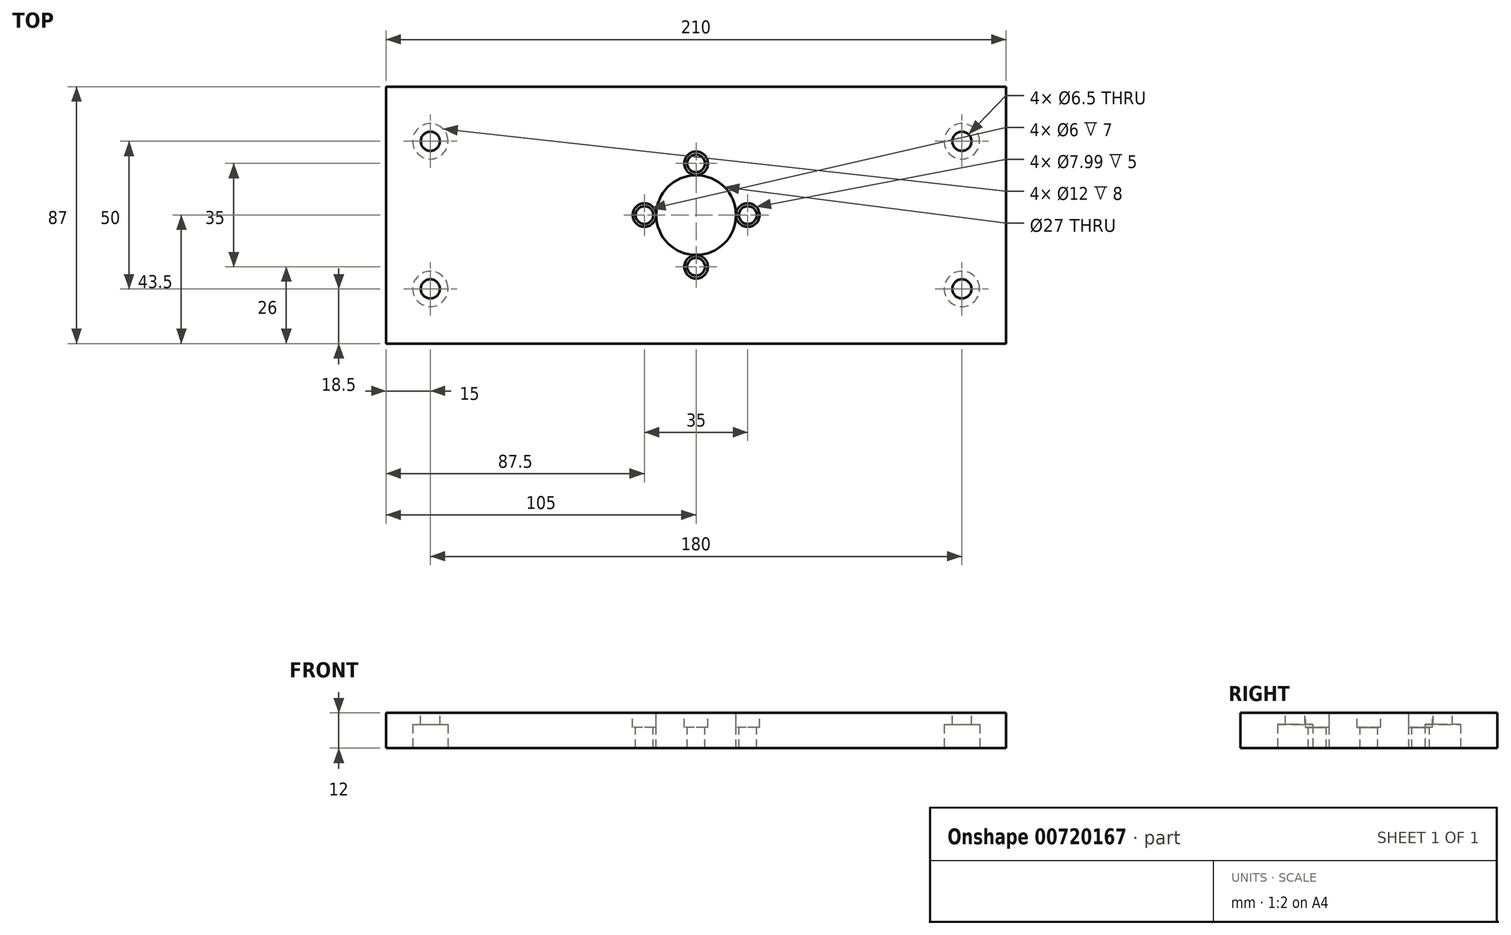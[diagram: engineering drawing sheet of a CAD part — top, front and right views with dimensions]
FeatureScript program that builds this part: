
annotation { "Feature Type Name" : "Feature", "Feature Type Description" : "" }
export const myFeature = defineFeature(function(context is Context, id is Id, definition is map)
    precondition{}
    {
        {
            var Q0;
            Q0=qCreatedBy(makeId("Top.planeOp"),FACE);
            var sketch = newSketch(context, id + "F0", { "sketchPlane" : qUnion([Q0])});
            skLineSegment(sketch, "E0.bottom", {"start": v(0, 0) * mm, "end": v(210, 0) * mm});
            skLineSegment(sketch, "E0.top", {"start": v(0, 87) * mm, "end": v(210, 87) * mm});
            skLineSegment(sketch, "E0.left", {"start": v(0, 0) * mm, "end": v(0, 87) * mm});
            skLineSegment(sketch, "E0.right", {"start": v(210, 0) * mm, "end": v(210, 87) * mm});
            skSolve(sketch);
        }
        {
            var Q0;
            Q0=makeQuery(id+"F0.imprint","IMPRINT",FACE,{"disambiguationData":[TD([[makeQuery(id+"F0.imprint","IMPRINT",EDGE,{"derivedFrom":sQuery(id+"F0.wireOp",EDGE,"E0.bottom")}),1.0]])]});
            extrude(context, id + "F1", {"entities" : qUnion([Q0]), "depth" : 12 * mm, "offsetDistance" : 25 * mm});
        }
        {
            var Q0;
            Q0=makeQuery(id+"F1.opExtrude","CAP_FACE",FACE,{"disambiguationData":[OSD([sQuery(id+"F0.wireOp",EDGE,"E0.bottom"),sQuery(id+"F0.wireOp",EDGE,"E0.top"),sQuery(id+"F0.wireOp",EDGE,"E0.left"),sQuery(id+"F0.wireOp",EDGE,"E0.right")])],"isStart":false});
            var sketch = newSketch(context, id + "F2", { "sketchPlane" : qUnion([Q0])});
            skCircle(sketch, "E1", {"center": v(15, 68.5) * mm, "radius": 3.25 * mm});
            skCircle(sketch, "E2", {"center": v(195, 68.5) * mm, "radius": 3.25 * mm});
            skCircle(sketch, "E3", {"center": v(195, 18.5) * mm, "radius": 3.25 * mm});
            skPoint(sketch, "E4.center.orphan", {"position": v(15, 18.5) * mm});
            skCircle(sketch, "E5", {"center": v(15, 18.5) * mm, "radius": 3.25 * mm});
            skSolve(sketch);
        }
        {
            var Q0;
            Q0 = qSketchRegion(id + "F2", true);
            extrude(context, id + "F3", {"entities" : qUnion([Q0]), "operationType" : NewBodyOperationType.REMOVE, "endBound" : BoundingType.THROUGH_ALL, "oppositeDirection" : true, "depth" : 25 * mm, "offsetDistance" : 25 * mm});
        }
        {
            var Q0;
            Q0=makeQuery(id+"F1.opExtrude","CAP_FACE",FACE,{"disambiguationData":[OSD([sQuery(id+"F0.wireOp",EDGE,"E0.bottom"),sQuery(id+"F0.wireOp",EDGE,"E0.top"),sQuery(id+"F0.wireOp",EDGE,"E0.left"),sQuery(id+"F0.wireOp",EDGE,"E0.right")])],"isStart":false});
            var sketch = newSketch(context, id + "F4", { "sketchPlane" : qUnion([Q0])});
            skCircle(sketch, "E6", {"center": v(105, 43.5) * mm, "radius": 13.5 * mm});
            skPoint(sketch, "E6.centerSnap0", {"position": v(210, 43.5) * mm});
            skPoint(sketch, "E6.centerSnap1", {"position": v(105, 87) * mm});
            skSolve(sketch);
        }
        {
            var Q0;
            Q0=makeQuery(id+"F4.imprint","IMPRINT",FACE,{"disambiguationData":[TD([[makeQuery(id+"F4.imprint","IMPRINT",EDGE,{"derivedFrom":sQuery(id+"F4.wireOp",EDGE,"E6")}),1.0]])]});
            extrude(context, id + "F5", {"entities" : qUnion([Q0]), "operationType" : NewBodyOperationType.REMOVE, "endBound" : BoundingType.THROUGH_ALL, "oppositeDirection" : true, "depth" : 25 * mm, "offsetDistance" : 25 * mm});
        }
        {
            var Q0;
            Q0=makeQuery(id+"F1.opExtrude","CAP_FACE",FACE,{"disambiguationData":[OSD([sQuery(id+"F0.wireOp",EDGE,"E0.bottom"),sQuery(id+"F0.wireOp",EDGE,"E0.top"),sQuery(id+"F0.wireOp",EDGE,"E0.left"),sQuery(id+"F0.wireOp",EDGE,"E0.right")])],"isStart":false});
            var sketch = newSketch(context, id + "F6", { "sketchPlane" : qUnion([Q0])});
            skCircle(sketch, "E7", {"center": v(105, 43.5) * mm, "radius": 17.5 * mm, "construction": true});
            skCircle(sketch, "E8", {"center": v(105, 61) * mm, "radius": 3 * mm});
            skCircle(sketch, "E9.1.0", {"center": v(87.5, 43.5) * mm, "radius": 3 * mm});
            skCircle(sketch, "E9.2.0", {"center": v(105, 26) * mm, "radius": 3 * mm});
            skCircle(sketch, "E9.3.0", {"center": v(122.5, 43.5) * mm, "radius": 3 * mm});
            skSolve(sketch);
        }
        {
            var Q0;
            Q0 = qSketchRegion(id + "F6", true);
            extrude(context, id + "F7", {"entities" : qUnion([Q0]), "operationType" : NewBodyOperationType.REMOVE, "endBound" : BoundingType.THROUGH_ALL, "oppositeDirection" : true, "depth" : 25 * mm, "offsetDistance" : 25 * mm});
        }
        {
            var Q0;
            Q0=makeQuery(id+"F1.opExtrude","CAP_FACE",FACE,{"disambiguationData":[OSD([sQuery(id+"F0.wireOp",EDGE,"E0.bottom"),sQuery(id+"F0.wireOp",EDGE,"E0.top"),sQuery(id+"F0.wireOp",EDGE,"E0.left"),sQuery(id+"F0.wireOp",EDGE,"E0.right")])],"isStart":false});
            var sketch = newSketch(context, id + "F8", { "sketchPlane" : qUnion([Q0])});
            skCircle(sketch, "E10", {"center": v(105, 61) * mm, "radius": 4 * mm});
            skCircle(sketch, "E11.1.0", {"center": v(87.5, 43.5) * mm, "radius": 4 * mm});
            skCircle(sketch, "E11.2.0", {"center": v(105, 26) * mm, "radius": 4 * mm});
            skCircle(sketch, "E11.3.0", {"center": v(122.5, 43.5) * mm, "radius": 4 * mm});
            skPoint(sketch, "E11.center", {"position": v(105, 43.5) * mm});
            skSolve(sketch);
        }
        {
            var Q0;
            Q0 = qSketchRegion(id + "F8", true);
            extrude(context, id + "F9", {"entities" : qUnion([Q0]), "operationType" : NewBodyOperationType.REMOVE, "oppositeDirection" : true, "depth" : 5 * mm, "offsetDistance" : 25 * mm});
        }
        {
            var Q0;
            Q0=makeQuery(id+"F1.opExtrude","CAP_FACE",FACE,{"disambiguationData":[OSD([sQuery(id+"F0.wireOp",EDGE,"E0.bottom"),sQuery(id+"F0.wireOp",EDGE,"E0.top"),sQuery(id+"F0.wireOp",EDGE,"E0.left"),sQuery(id+"F0.wireOp",EDGE,"E0.right")])],"isStart":true});
            var sketch = newSketch(context, id + "F10", { "sketchPlane" : qUnion([Q0])});
            skCircle(sketch, "E12", {"center": v(15, -18.5) * mm, "radius": 6 * mm});
            skCircle(sketch, "E13.0.1.0", {"center": v(15, -68.5) * mm, "radius": 6 * mm});
            skCircle(sketch, "E13.1.0.0", {"center": v(195, -18.5) * mm, "radius": 6 * mm});
            skCircle(sketch, "E13.1.1.0", {"center": v(195, -68.5) * mm, "radius": 6 * mm});
            skLineSegment(sketch, "E13.direction1", {"start": v(15, -18.5) * mm, "end": v(195, -18.5) * mm, "construction": true});
            skLineSegment(sketch, "E13.direction2", {"start": v(15, -18.5) * mm, "end": v(15, -68.5) * mm, "construction": true});
            skSolve(sketch);
        }
        {
            var Q0;
            Q0 = qSketchRegion(id + "F10", true);
            extrude(context, id + "F11", {"entities" : qUnion([Q0]), "operationType" : NewBodyOperationType.REMOVE, "oppositeDirection" : true, "depth" : 8 * mm, "offsetDistance" : 25 * mm});
        }
    });
